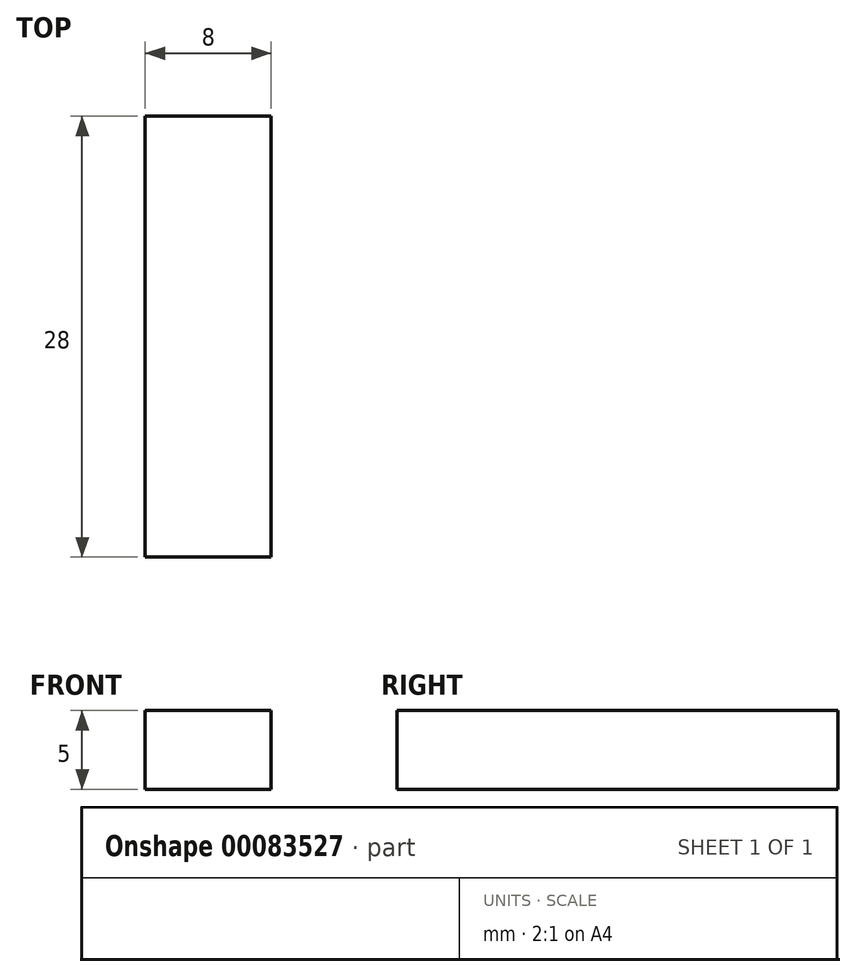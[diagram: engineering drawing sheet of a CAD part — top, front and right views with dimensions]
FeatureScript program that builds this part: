
annotation { "Feature Type Name" : "Feature", "Feature Type Description" : "" }
export const myFeature = defineFeature(function(context is Context, id is Id, definition is map)
    precondition{}
    {
        {
            var Q0;
            Q0=qCreatedBy(makeId("Top.planeOp"),FACE);
            var sketch = newSketch(context, id + "F0", { "sketchPlane" : qUnion([Q0])});
            skLineSegment(sketch, "E0.bottom", {"start": v(-5.06, 5.8) * mm, "end": v(2.94, 5.8) * mm});
            skLineSegment(sketch, "E0.top", {"start": v(-5.06, -22.2) * mm, "end": v(2.94, -22.2) * mm});
            skLineSegment(sketch, "E0.left", {"start": v(-5.06, 5.8) * mm, "end": v(-5.06, -22.2) * mm});
            skLineSegment(sketch, "E0.right", {"start": v(2.94, 5.8) * mm, "end": v(2.94, -22.2) * mm});
            skSolve(sketch);
        }
        {
            var Q0;
            Q0 = qSketchRegion(id + "F0", true);
            extrude(context, id + "F1", {"entities" : qUnion([Q0]), "depth" : 5 * mm});
        }
    });
